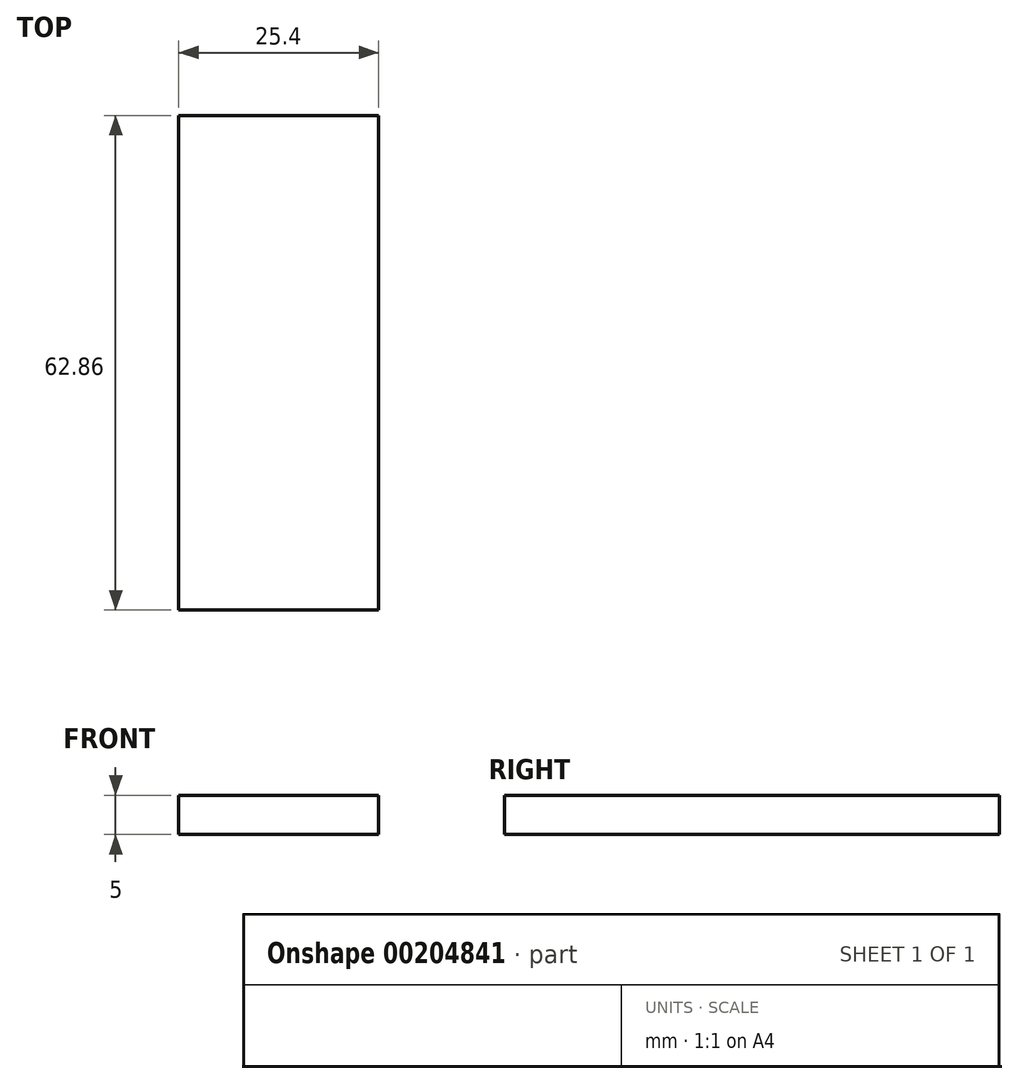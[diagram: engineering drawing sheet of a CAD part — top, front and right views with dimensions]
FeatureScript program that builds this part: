
annotation { "Feature Type Name" : "Feature", "Feature Type Description" : "" }
export const myFeature = defineFeature(function(context is Context, id is Id, definition is map)
    precondition{}
    {
        {
            var Q0;
            Q0=qCreatedBy(makeId("Top.planeOp"),FACE);
            var sketch = newSketch(context, id + "F0", { "sketchPlane" : qUnion([Q0])});
            skLineSegment(sketch, "E0.bottom", {"start": v(12.7, 31.43) * mm, "end": v(-12.7, 31.43) * mm});
            skLineSegment(sketch, "E0.top", {"start": v(12.7, -31.43) * mm, "end": v(-12.7, -31.43) * mm});
            skLineSegment(sketch, "E0.left", {"start": v(12.7, 31.43) * mm, "end": v(12.7, -31.43) * mm});
            skLineSegment(sketch, "E0.right", {"start": v(-12.7, 31.43) * mm, "end": v(-12.7, -31.43) * mm});
            skPoint(sketch, "E0.middle", {"position": v(0, 0) * mm});
            skSolve(sketch);
        }
        {
            var Q0;
            Q0=makeQuery(id+"F0.imprint","IMPRINT",FACE,{"disambiguationData":[TD([[makeQuery(id+"F0.imprint","IMPRINT",EDGE,{"derivedFrom":sQuery(id+"F0.wireOp",EDGE,"E0.bottom")}),1.0]])]});
            extrude(context, id + "F1", {"entities" : qUnion([Q0]), "depth" : 5 * mm});
        }
    });
